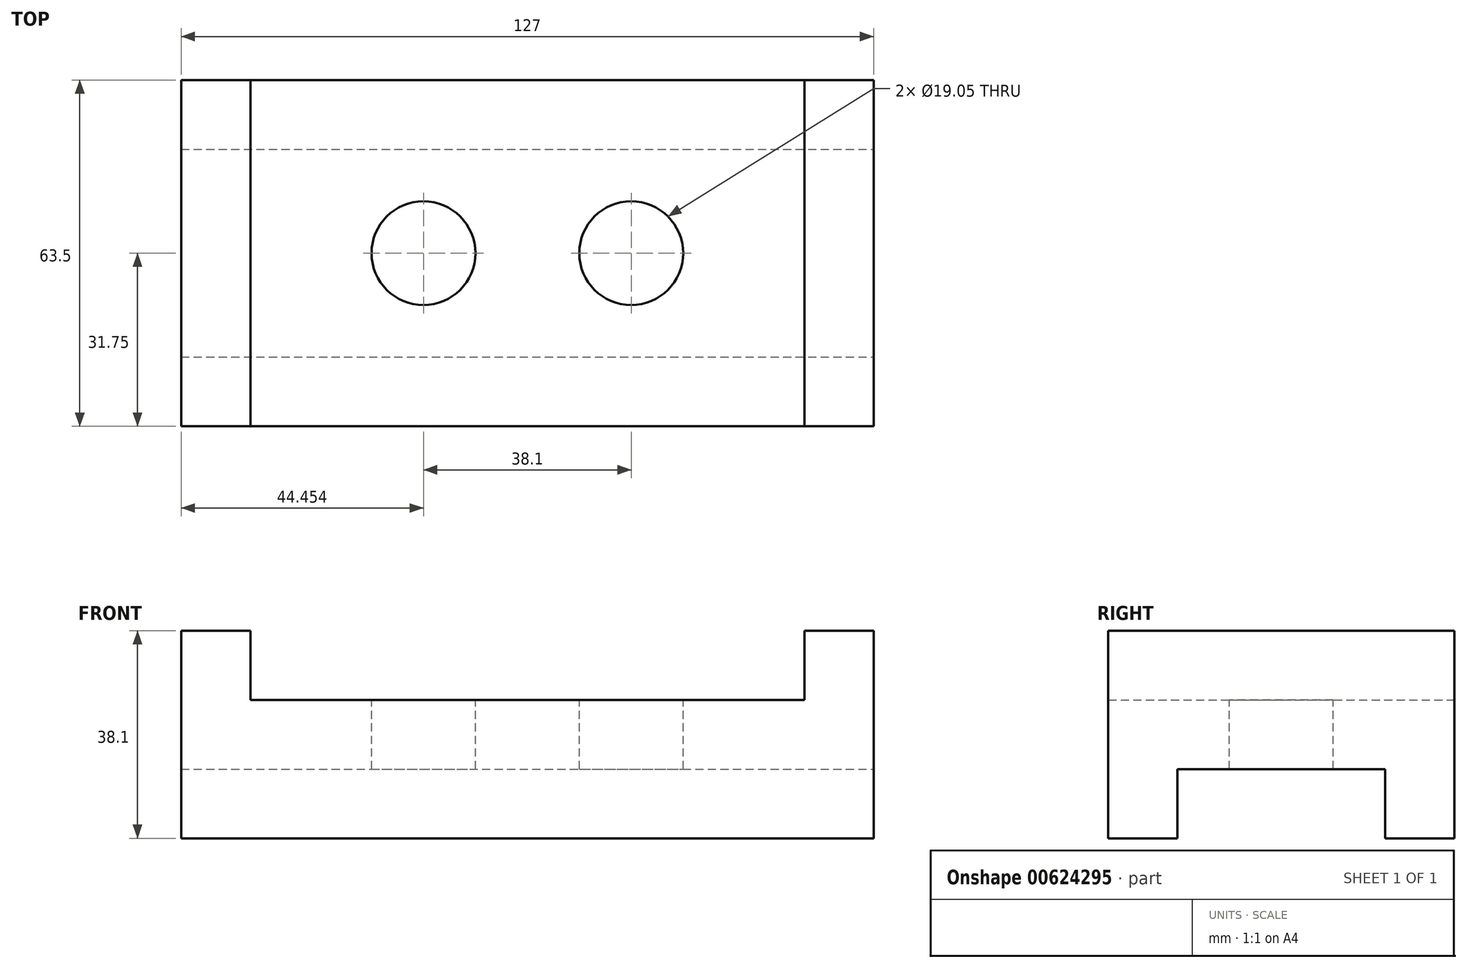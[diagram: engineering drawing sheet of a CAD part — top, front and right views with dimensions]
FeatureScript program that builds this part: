
annotation { "Feature Type Name" : "Feature", "Feature Type Description" : "" }
export const myFeature = defineFeature(function(context is Context, id is Id, definition is map)
    precondition{}
    {
        {
            var Q0;
            Q0=qCreatedBy(makeId("Front.planeOp"),FACE);
            var sketch = newSketch(context, id + "F0", { "sketchPlane" : qUnion([Q0])});
            skLineSegment(sketch, "E0", {"start": v(-85.55, -75.44) * mm, "end": v(41.45, -75.44) * mm});
            skLineSegment(sketch, "E1", {"start": v(41.45, -75.44) * mm, "end": v(41.45, -37.34) * mm});
            skLineSegment(sketch, "E2", {"start": v(41.45, -37.34) * mm, "end": v(28.75, -37.34) * mm});
            skLineSegment(sketch, "E3", {"start": v(28.75, -37.34) * mm, "end": v(28.75, -50.04) * mm});
            skLineSegment(sketch, "E4", {"start": v(28.75, -50.04) * mm, "end": v(-72.85, -50.04) * mm});
            skLineSegment(sketch, "E5", {"start": v(-72.85, -50.04) * mm, "end": v(-72.85, -37.34) * mm});
            skLineSegment(sketch, "E6", {"start": v(-72.85, -37.34) * mm, "end": v(-85.55, -37.34) * mm});
            skLineSegment(sketch, "E7", {"start": v(-85.55, -37.34) * mm, "end": v(-85.55, -75.44) * mm});
            skSolve(sketch);
        }
        {
            var Q0;
            Q0=makeQuery(id+"F0.imprint","IMPRINT",FACE,{"disambiguationData":[TD([[makeQuery(id+"F0.imprint","IMPRINT",EDGE,{"derivedFrom":sQuery(id+"F0.wireOp",EDGE,"E0")}),1.0]])]});
            extrude(context, id + "F1", {"entities" : qUnion([Q0]), "depth" : 63.5 * mm, "offsetDistance" : 25.4 * mm});
        }
        {
            var Q0;
            Q0=makeQuery(id+"F1.opExtrude","SWEPT_FACE",FACE,{"disambiguationData":[OSD([sQuery(id+"F0.wireOp",EDGE,"E1")])]});
            var sketch = newSketch(context, id + "F2", { "sketchPlane" : qUnion([Q0])});
            skLineSegment(sketch, "E8", {"start": v(-63.5, -75.44) * mm, "end": v(-50.8, -75.44) * mm});
            skLineSegment(sketch, "E9", {"start": v(-50.8, -75.44) * mm, "end": v(-50.8, -62.74) * mm});
            skLineSegment(sketch, "E10", {"start": v(-50.8, -62.74) * mm, "end": v(-12.7, -62.74) * mm});
            skLineSegment(sketch, "E11", {"start": v(-12.7, -62.74) * mm, "end": v(-12.7, -75.44) * mm});
            skLineSegment(sketch, "E12", {"start": v(-12.7, -75.44) * mm, "end": v(0, -75.44) * mm});
            skSolve(sketch);
        }
        {
            var Q0;
            {var subQ0=sQuery(id+"F2.wireOp",EDGE,"E9");Q0=makeQuery(id+"F2.imprint","IMPRINT",FACE,{"disambiguationData":[TD([[makeQuery(id+"F2.imprint","IMPRINT",EDGE,{"derivedFrom":subQ0}),-1.0]])]});}
            extrude(context, id + "F3", {"entities" : qUnion([Q0]), "operationType" : NewBodyOperationType.REMOVE, "oppositeDirection" : true, "depth" : 254 * mm, "offsetDistance" : 25.4 * mm});
        }
        {
            var Q0;
            Q0=makeQuery(id+"F1.opExtrude","SWEPT_FACE",FACE,{"disambiguationData":[OSD([sQuery(id+"F0.wireOp",EDGE,"E6")])]});
            var sketch = newSketch(context, id + "F4", { "sketchPlane" : qUnion([Q0])});
            skPoint(sketch, "E13.endSnap0", {"position": v(-79.2, -63.5) * mm});
            skCircle(sketch, "E14", {"center": v(-41.1, -31.75) * mm, "radius": 9.53 * mm});
            skCircle(sketch, "E15", {"center": v(-3, -31.75) * mm, "radius": 9.53 * mm});
            skSolve(sketch);
        }
        {
            var Q0;
            Q0 = qSketchRegion(id + "F4", true);
            extrude(context, id + "F5", {"entities" : qUnion([Q0]), "operationType" : NewBodyOperationType.REMOVE, "oppositeDirection" : true, "depth" : 203.2 * mm, "offsetDistance" : 25.4 * mm});
        }
    });
